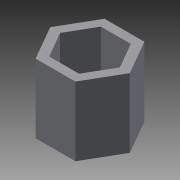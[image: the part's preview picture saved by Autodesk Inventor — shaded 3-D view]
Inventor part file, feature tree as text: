
AUTODESK INVENTOR PART (.ipt)
format: ipt  version: 2013 (Build 170138000, 138)  size: 77,312 bytes
history: native  units: in
note: dims shown in document units (in); Inventor stores cm internally (conversion verified against a paired STEP export)
features: extrude x1, sketch x1
ambient origin geometry x8: Origin, YZ Plane, XZ Plane, XY Plane, X Axis, Y Axis, Z Axis, Center Point
bodies: Solid1 (feature_tree)
feature tree (2):
  extrude  "Extrusion1"  Depth=0.375in
  sketch  "Sketch1"  dims[d1=0.5in d2=0.375in d3=0.5in d4=0.0in]
